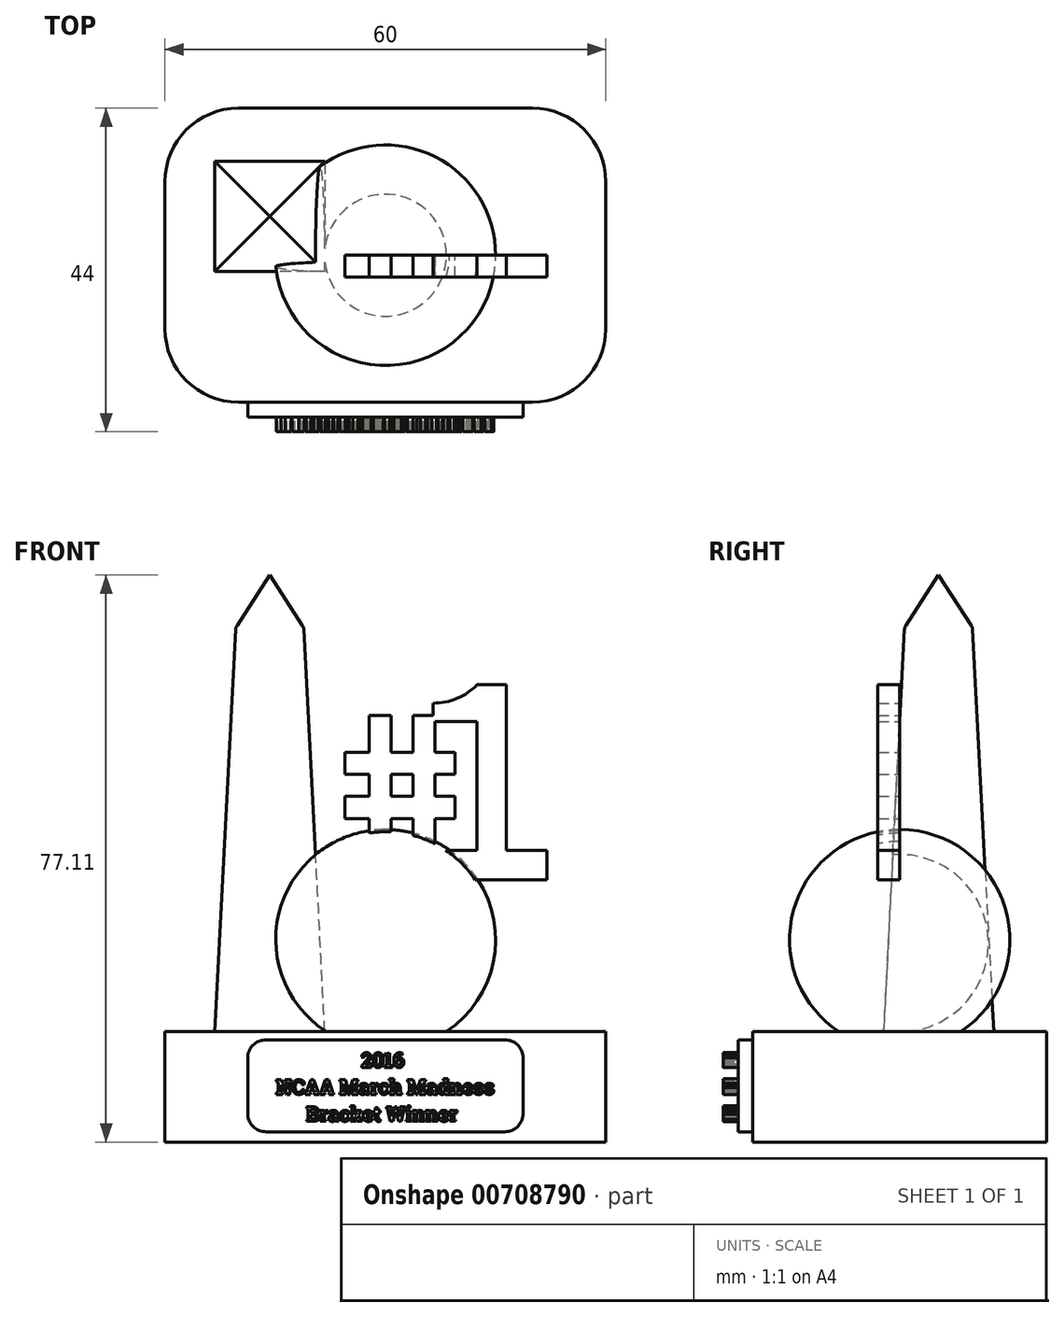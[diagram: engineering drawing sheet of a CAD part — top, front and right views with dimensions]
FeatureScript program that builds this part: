
annotation { "Feature Type Name" : "Feature", "Feature Type Description" : "" }
export const myFeature = defineFeature(function(context is Context, id is Id, definition is map)
    precondition{}
    {
        {
            var Q0;
            Q0=qCreatedBy(makeId("Top.planeOp"),FACE);
            var sketch = newSketch(context, id + "F0", { "sketchPlane" : qUnion([Q0])});
            skLineSegment(sketch, "E0.bottom", {"start": v(20, -20) * mm, "end": v(-20, -20) * mm});
            skLineSegment(sketch, "E0.top", {"start": v(20, 20) * mm, "end": v(-20, 20) * mm});
            skLineSegment(sketch, "E0.left", {"start": v(30, -10) * mm, "end": v(30, 10) * mm});
            skLineSegment(sketch, "E0.right", {"start": v(-30, -10) * mm, "end": v(-30, 10) * mm});
            skPoint(sketch, "E0.middle", {"position": v(0, 0) * mm});
            skPoint(sketch, "E1.visualSharp", {"position": v(-30, 20) * mm});
            skArc(sketch, "E1.filletArc", {"start": v(-20, 20) * mm, "mid": v(-27.07, 17.07) * mm, "end": v(-30, 10) * mm});
            skPoint(sketch, "E2.visualSharp", {"position": v(30, 20) * mm});
            skArc(sketch, "E2.filletArc", {"start": v(30, 10) * mm, "mid": v(27.07, 17.07) * mm, "end": v(20, 20) * mm});
            skPoint(sketch, "E3.visualSharp", {"position": v(-30, -20) * mm});
            skArc(sketch, "E3.filletArc", {"start": v(-30, -10) * mm, "mid": v(-27.07, -17.07) * mm, "end": v(-20, -20) * mm});
            skPoint(sketch, "E4.visualSharp", {"position": v(30, -20) * mm});
            skArc(sketch, "E4.filletArc", {"start": v(20, -20) * mm, "mid": v(27.07, -17.07) * mm, "end": v(30, -10) * mm});
            skSolve(sketch);
        }
        {
            var Q0;
            Q0=makeQuery(id+"F0.imprint","IMPRINT",FACE,{"disambiguationData":[TD([[makeQuery(id+"F0.imprint","IMPRINT",EDGE,{"derivedFrom":sQuery(id+"F0.wireOp",EDGE,"E0.bottom")}),-1.0]])]});
            extrude(context, id + "F1", {"entities" : qUnion([Q0]), "depth" : 15 * mm, "offsetDistance" : 25 * mm});
        }
        {
            var Q0;
            Q0=makeQuery(id+"F1.opExtrude","CAP_FACE",FACE,{"disambiguationData":[OSD([sQuery(id+"F0.wireOp",EDGE,"E0.bottom"),sQuery(id+"F0.wireOp",EDGE,"E0.top"),sQuery(id+"F0.wireOp",EDGE,"E0.left"),sQuery(id+"F0.wireOp",EDGE,"E0.right"),sQuery(id+"F0.wireOp",EDGE,"E1.filletArc"),sQuery(id+"F0.wireOp",EDGE,"E2.filletArc"),sQuery(id+"F0.wireOp",EDGE,"E3.filletArc"),sQuery(id+"F0.wireOp",EDGE,"E4.filletArc")])],"isStart":false});
            var sketch = newSketch(context, id + "F2", { "sketchPlane" : qUnion([Q0])});
            skLineSegment(sketch, "E5.bottom", {"start": v(-8.24, -2.22) * mm, "end": v(-23.24, -2.22) * mm});
            skLineSegment(sketch, "E5.top", {"start": v(-8.24, 12.78) * mm, "end": v(-23.24, 12.78) * mm});
            skLineSegment(sketch, "E5.left", {"start": v(-8.24, -2.22) * mm, "end": v(-8.24, 12.78) * mm});
            skLineSegment(sketch, "E5.right", {"start": v(-23.24, -2.22) * mm, "end": v(-23.24, 12.78) * mm});
            skPoint(sketch, "E5.middle", {"position": v(-15.74, 5.28) * mm});
            skSolve(sketch);
        }
        {
            var Q0;
            Q0 = qSketchRegion(id + "F2", true);
            extrude(context, id + "F3", {"entities" : qUnion([Q0]), "operationType" : NewBodyOperationType.ADD, "depth" : 55 * mm, "offsetDistance" : 25 * mm, "hasDraft" : true, "draftAngle" : 3 * degree, "draftPullDirection" : true});
        }
        {
            var Q0;
            Q0=makeQuery(id+"F3.opExtrude","CAP_FACE",FACE,{"disambiguationData":[OSD([sQuery(id+"F2.wireOp",EDGE,"E5.bottom"),sQuery(id+"F2.wireOp",EDGE,"E5.top"),sQuery(id+"F2.wireOp",EDGE,"E5.left"),sQuery(id+"F2.wireOp",EDGE,"E5.right")])],"isStart":false});
            var sketch = newSketch(context, id + "F4", { "sketchPlane" : qUnion([Q0])});
            skLineSegment(sketch, "E6.bottom", {"start": v(-20.36, 9.9) * mm, "end": v(-11.12, 9.9) * mm});
            skLineSegment(sketch, "E6.top", {"start": v(-20.36, 0.67) * mm, "end": v(-11.12, 0.67) * mm});
            skLineSegment(sketch, "E6.left", {"start": v(-20.36, 9.9) * mm, "end": v(-20.36, 0.67) * mm});
            skLineSegment(sketch, "E6.right", {"start": v(-11.12, 9.9) * mm, "end": v(-11.12, 0.67) * mm});
            skSolve(sketch);
        }
        {
            var Q0;
            Q0 = qSketchRegion(id + "F4", true);
            extrude(context, id + "F5", {"entities" : qUnion([Q0]), "operationType" : NewBodyOperationType.ADD, "depth" : 7.5 * mm, "offsetDistance" : 25 * mm, "hasDraft" : true, "draftAngle" : 33 * degree, "draftPullDirection" : true});
        }
        {
            var Q0;
            Q0=makeQuery(id+"F1.opExtrude","SWEPT_FACE",FACE,{"disambiguationData":[OSD([sQuery(id+"F0.wireOp",EDGE,"E0.bottom")])]});
            var sketch = newSketch(context, id + "F6", { "sketchPlane" : qUnion([Q0])});
            skLineSegment(sketch, "E7.bottom", {"start": v(16.25, 1.4) * mm, "end": v(-16.25, 1.4) * mm});
            skLineSegment(sketch, "E7.top", {"start": v(16.25, 13.9) * mm, "end": v(-16.25, 13.9) * mm});
            skLineSegment(sketch, "E7.left", {"start": v(18.75, 3.9) * mm, "end": v(18.75, 11.4) * mm});
            skLineSegment(sketch, "E7.right", {"start": v(-18.75, 3.9) * mm, "end": v(-18.75, 11.4) * mm});
            skPoint(sketch, "E7.middle", {"position": v(0, 7.65) * mm});
            skPoint(sketch, "E8.visualSharp", {"position": v(-18.75, 13.9) * mm});
            skArc(sketch, "E8.filletArc", {"start": v(-16.25, 13.9) * mm, "mid": v(-18.02, 13.16) * mm, "end": v(-18.75, 11.4) * mm});
            skPoint(sketch, "E9.visualSharp", {"position": v(-18.75, 1.4) * mm});
            skArc(sketch, "E9.filletArc", {"start": v(-18.75, 3.9) * mm, "mid": v(-18.02, 2.13) * mm, "end": v(-16.25, 1.4) * mm});
            skPoint(sketch, "E10.visualSharp", {"position": v(18.75, 1.4) * mm});
            skArc(sketch, "E10.filletArc", {"start": v(16.25, 1.4) * mm, "mid": v(18.02, 2.13) * mm, "end": v(18.75, 3.9) * mm});
            skPoint(sketch, "E11.visualSharp", {"position": v(18.75, 13.9) * mm});
            skArc(sketch, "E11.filletArc", {"start": v(18.75, 11.4) * mm, "mid": v(18.02, 13.16) * mm, "end": v(16.25, 13.9) * mm});
            skSolve(sketch);
        }
        {
            var Q0;
            Q0=makeQuery(id+"F6.imprint","IMPRINT",FACE,{"disambiguationData":[TD([[makeQuery(id+"F6.imprint","IMPRINT",EDGE,{"derivedFrom":sQuery(id+"F6.wireOp",EDGE,"E7.bottom")}),-1.0]])]});
            extrude(context, id + "F7", {"entities" : qUnion([Q0]), "operationType" : NewBodyOperationType.ADD, "depth" : 2 * mm, "offsetDistance" : 25 * mm});
        }
        {
            var Q0;
            Q0=makeQuery(id+"F7.opExtrude","CAP_FACE",FACE,{"disambiguationData":[OSD([sQuery(id+"F6.wireOp",EDGE,"E7.bottom"),sQuery(id+"F6.wireOp",EDGE,"E7.top"),sQuery(id+"F6.wireOp",EDGE,"E7.left"),sQuery(id+"F6.wireOp",EDGE,"E7.right"),sQuery(id+"F6.wireOp",EDGE,"E8.filletArc"),sQuery(id+"F6.wireOp",EDGE,"E9.filletArc"),sQuery(id+"F6.wireOp",EDGE,"E10.filletArc"),sQuery(id+"F6.wireOp",EDGE,"E11.filletArc")])],"isStart":false});
            var sketch = newSketch(context, id + "F8", { "sketchPlane" : qUnion([Q0])});
            skText(sketch, "E12", { "text": "                 2016 \nNCAA March Madness \n      Bracket Winner", "fontName": "RobotoSlab-Bold.ttf"});
            const initialGuessF8  = {"E12": [-0.0149, 0.01015, 1, 0, 0.002]};
            skSetInitialGuess(sketch, initialGuessF8);
            skSolve(sketch);
        }
        {
            var Q0;
            Q0 = qSketchRegion(id + "F8", true);
            extrude(context, id + "F9", {"entities" : qUnion([Q0]), "operationType" : NewBodyOperationType.ADD, "depth" : 2 * mm, "offsetDistance" : 25 * mm});
        }
        {
            var Q0;
            Q0=makeQuery(id+"F5.boolean.opBoolean","MERGE",EDGE,{"derivedFrom":[makeQuery(id+"F3.opExtrude","CAP_EDGE",EDGE,{"disambiguationData":[OSD([sQuery(id+"F2.wireOp",EDGE,"E5.bottom")])],"isStart":false}),makeQuery(id+"F5.opExtrude","CAP_EDGE",EDGE,{"disambiguationData":[OSD([sQuery(id+"F4.wireOp",EDGE,"E6.top")])],"isStart":true})]});
            var Q1;
            Q1=makeQuery(id+"F5.boolean.opBoolean","MERGE",EDGE,{"derivedFrom":[makeQuery(id+"F3.opExtrude","CAP_EDGE",EDGE,{"disambiguationData":[OSD([sQuery(id+"F2.wireOp",EDGE,"E5.left")])],"isStart":false}),makeQuery(id+"F5.opExtrude","CAP_EDGE",EDGE,{"disambiguationData":[OSD([sQuery(id+"F4.wireOp",EDGE,"E6.right")])],"isStart":true})]});
            var Q2;
            Q2=makeQuery(id+"F5.boolean.opBoolean","MERGE",EDGE,{"derivedFrom":[makeQuery(id+"F3.opExtrude","CAP_EDGE",EDGE,{"disambiguationData":[OSD([sQuery(id+"F2.wireOp",EDGE,"E5.top")])],"isStart":false}),makeQuery(id+"F5.opExtrude","CAP_EDGE",EDGE,{"disambiguationData":[OSD([sQuery(id+"F4.wireOp",EDGE,"E6.bottom")])],"isStart":true})]});
            var Q3;
            Q3=makeQuery(id+"F5.boolean.opBoolean","MERGE",EDGE,{"derivedFrom":[makeQuery(id+"F3.opExtrude","CAP_EDGE",EDGE,{"disambiguationData":[OSD([sQuery(id+"F2.wireOp",EDGE,"E5.right")])],"isStart":false}),makeQuery(id+"F5.opExtrude","CAP_EDGE",EDGE,{"disambiguationData":[OSD([sQuery(id+"F4.wireOp",EDGE,"E6.left")])],"isStart":true})]});
            fillet(context, id + "F10", {"entities" : qUnion([Q0, Q1, Q2, Q3]), "radius" : 1 * mm, "tangentPropagation" : true, "allowEdgeOverflow" : false});
        }
        {
            var Q0;
            Q0=qCreatedBy(makeId("Front.planeOp"),FACE);
            var sketch = newSketch(context, id + "F11", { "sketchPlane" : qUnion([Q0])});
            skArc(sketch, "E13", {"start": v(0, 12.5) * mm, "mid": v(15, 27.5) * mm, "end": v(0, 42.5) * mm});
            skLineSegment(sketch, "E14", {"start": v(0, 53.35) * mm, "end": v(0, 13.04) * mm, "construction": true});
            skLineSegment(sketch, "E15", {"start": v(0, 42.5) * mm, "end": v(0, 12.5) * mm});
            skSolve(sketch);
        }
        {
            var Q0;
            Q0 = qSketchRegion(id + "F11", true);
            var Q1;
            Q1=sQuery(id+"F11.wireOp",EDGE,"E13");
            var Q2;
            Q2=sQuery(id+"F11.wireOp",EDGE,"E15");
            var Q3;
            Q3=sQuery(id+"F11.wireOp",EDGE,"E14");
            revolve(context, id + "F12", {"operationType" : NewBodyOperationType.ADD, "surfaceOperationType" : NewSurfaceOperationType.NEW, "entities" : qUnion([Q0]), "surfaceEntities" : qUnion([Q1, Q2]), "axis" : qUnion([Q3]), "revolveType" : RevolveType.FULL});
        }
        {
            var Q0;
            Q0=qCreatedBy(makeId("Front.planeOp"),FACE);
            var sketch = newSketch(context, id + "F13", { "sketchPlane" : qUnion([Q0])});
            skLineSegment(sketch, "E16.bottom", {"start": v(6.99, 39.7) * mm, "end": v(12.49, 39.7) * mm});
            skLineSegment(sketch, "E16.top", {"start": v(6.99, 35.7) * mm, "end": v(21.99, 35.7) * mm});
            skLineSegment(sketch, "E16.left", {"start": v(6.99, 39.7) * mm, "end": v(6.99, 35.7) * mm});
            skLineSegment(sketch, "E16.right", {"start": v(21.99, 39.7) * mm, "end": v(21.99, 35.7) * mm});
            skLineSegment(sketch, "E17", {"start": v(12.49, 39.7) * mm, "end": v(12.49, 57.2) * mm});
            skLineSegment(sketch, "E18", {"start": v(16.49, 57.2) * mm, "end": v(16.49, 39.7) * mm});
            skLineSegment(sketch, "E19.top", {"start": v(16.49, 62.2) * mm, "end": v(12.49, 62.2) * mm});
            skLineSegment(sketch, "E19.left", {"start": v(16.49, 57.2) * mm, "end": v(16.49, 62.2) * mm});
            skLineSegment(sketch, "E20.top", {"start": v(12.49, 57.2) * mm, "end": v(6.49, 57.2) * mm});
            skLineSegment(sketch, "E20.right", {"start": v(6.49, 59.7) * mm, "end": v(6.49, 57.2) * mm});
            skLineSegment(sketch, "E21", {"start": v(14.49, 35.7) * mm, "end": v(14.49, 76.92) * mm, "construction": true});
            skArc(sketch, "E22", {"start": v(6.49, 59.7) * mm, "mid": v(9.74, 60.34) * mm, "end": v(12.49, 62.2) * mm});
            skPoint(sketch, "E23.orphan", {"position": v(6.49, 62.2) * mm});
            skLineSegment(sketch, "E24.trimOffspring", {"start": v(16.49, 39.7) * mm, "end": v(21.99, 39.7) * mm});
            skLineSegment(sketch, "E25.bottom", {"start": v(-2.23, 58) * mm, "end": v(0.77, 58) * mm});
            skLineSegment(sketch, "E25.top", {"start": v(-2.23, 38) * mm, "end": v(0.77, 38) * mm});
            skLineSegment(sketch, "E25.left", {"start": v(-5.52, 53) * mm, "end": v(-5.52, 50) * mm});
            skLineSegment(sketch, "E26.left", {"start": v(-2.23, 58) * mm, "end": v(-2.23, 53) * mm});
            skLineSegment(sketch, "E26.right", {"start": v(0.77, 58) * mm, "end": v(0.77, 53) * mm});
            skLineSegment(sketch, "E27.bottom", {"start": v(3.77, 58) * mm, "end": v(6.49, 58) * mm});
            skLineSegment(sketch, "E27.top", {"start": v(3.77, 38) * mm, "end": v(6.77, 38) * mm});
            skLineSegment(sketch, "E27.left", {"start": v(3.77, 58) * mm, "end": v(3.77, 53) * mm});
            skLineSegment(sketch, "E27.right", {"start": v(6.77, 57.2) * mm, "end": v(6.77, 53) * mm});
            skLineSegment(sketch, "E28.bottom", {"start": v(-5.52, 53) * mm, "end": v(-2.23, 53) * mm});
            skLineSegment(sketch, "E28.top", {"start": v(-5.52, 50) * mm, "end": v(-2.23, 50) * mm});
            skLineSegment(sketch, "E28.right", {"start": v(9.47, 53) * mm, "end": v(9.47, 50) * mm});
            skLineSegment(sketch, "E29.bottom", {"start": v(9.47, 44) * mm, "end": v(6.77, 44) * mm});
            skLineSegment(sketch, "E29.top", {"start": v(9.47, 47) * mm, "end": v(6.77, 47) * mm});
            skLineSegment(sketch, "E29.left", {"start": v(9.47, 44) * mm, "end": v(9.47, 47) * mm});
            skLineSegment(sketch, "E29.right", {"start": v(-5.52, 44) * mm, "end": v(-5.52, 47) * mm});
            skLineSegment(sketch, "E30.trimOffspring", {"start": v(9.47, 47) * mm, "end": v(9.47, 44) * mm});
            skLineSegment(sketch, "E31.trimOffspring", {"start": v(-5.52, 47) * mm, "end": v(-5.52, 44) * mm});
            skLineSegment(sketch, "E32.trimOffspring", {"start": v(6.77, 53) * mm, "end": v(9.47, 53) * mm});
            skLineSegment(sketch, "E33.trimOffspring", {"start": v(0.77, 53) * mm, "end": v(3.77, 53) * mm});
            skLineSegment(sketch, "E34.trimOffspring", {"start": v(-2.23, 50) * mm, "end": v(-2.23, 47) * mm});
            skLineSegment(sketch, "E35.trimOffspring", {"start": v(0.77, 50) * mm, "end": v(0.77, 47) * mm});
            skLineSegment(sketch, "E36.trimOffspring", {"start": v(3.77, 50) * mm, "end": v(3.77, 47) * mm});
            skLineSegment(sketch, "E37.trimOffspring", {"start": v(6.77, 50) * mm, "end": v(6.77, 47) * mm});
            skLineSegment(sketch, "E38.trimOffspring", {"start": v(-2.23, 47) * mm, "end": v(-5.52, 47) * mm});
            skLineSegment(sketch, "E39.trimOffspring", {"start": v(0.77, 50) * mm, "end": v(3.77, 50) * mm});
            skLineSegment(sketch, "E40.trimOffspring", {"start": v(6.77, 50) * mm, "end": v(9.47, 50) * mm});
            skLineSegment(sketch, "E41.trimOffspring", {"start": v(3.77, 47) * mm, "end": v(0.77, 47) * mm});
            skLineSegment(sketch, "E42.trimOffspring", {"start": v(3.77, 44) * mm, "end": v(0.77, 44) * mm});
            skLineSegment(sketch, "E43.trimOffspring", {"start": v(6.77, 44) * mm, "end": v(6.77, 38) * mm});
            skLineSegment(sketch, "E44.trimOffspring", {"start": v(3.77, 44) * mm, "end": v(3.77, 38) * mm});
            skLineSegment(sketch, "E45.trimOffspring", {"start": v(0.77, 44) * mm, "end": v(0.77, 38) * mm});
            skLineSegment(sketch, "E46.trimOffspring", {"start": v(-2.23, 44) * mm, "end": v(-2.23, 38) * mm});
            skLineSegment(sketch, "E47.trimOffspring", {"start": v(-2.23, 44) * mm, "end": v(-5.52, 44) * mm});
            skSolve(sketch);
        }
        {
            var Q0;
            Q0 = qSketchRegion(id + "F13", true);
            extrude(context, id + "F14", {"entities" : qUnion([Q0]), "operationType" : NewBodyOperationType.ADD, "depth" : 3 * mm, "offsetDistance" : 25 * mm});
        }
    });
